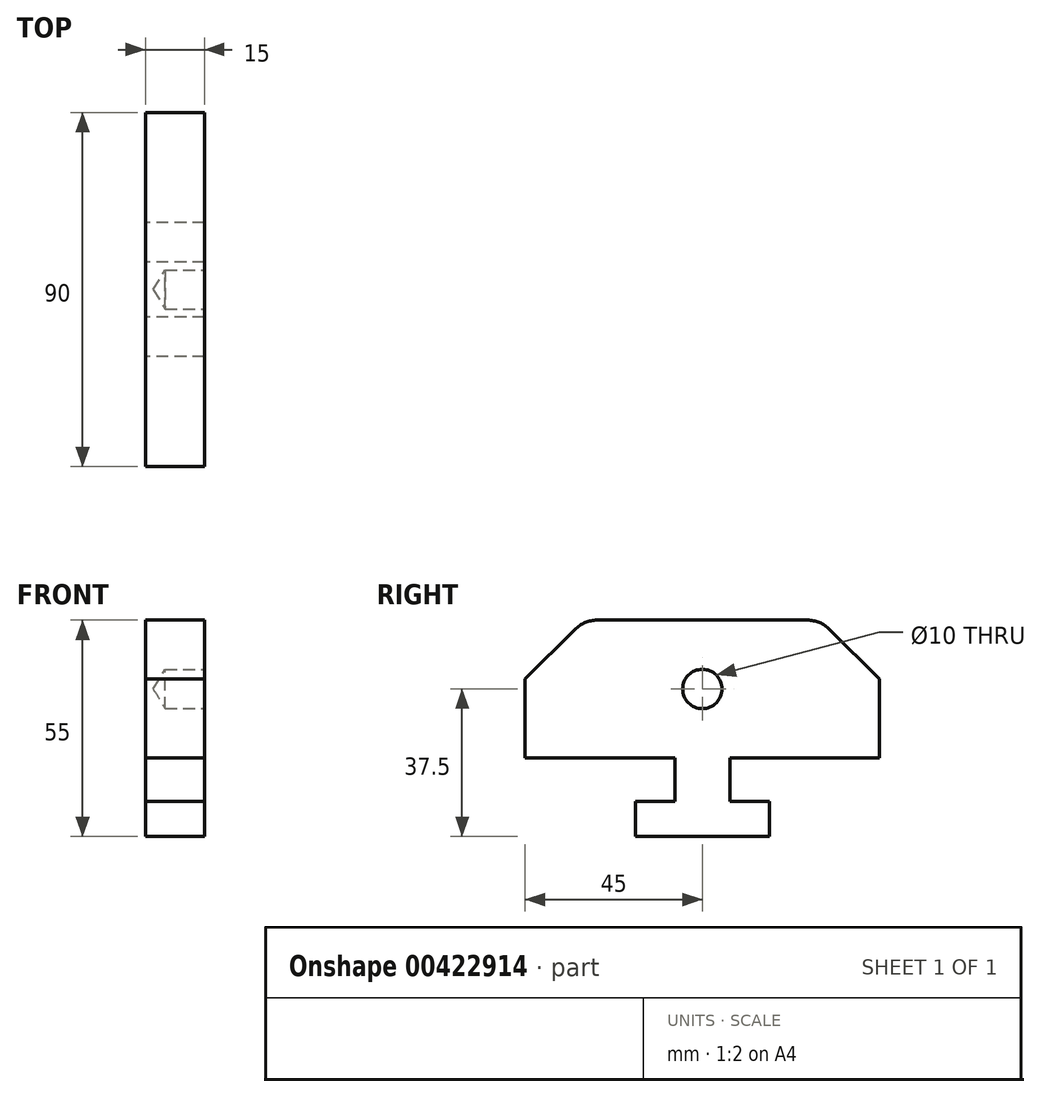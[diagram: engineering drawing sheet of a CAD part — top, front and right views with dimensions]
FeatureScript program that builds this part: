
annotation { "Feature Type Name" : "Feature", "Feature Type Description" : "" }
export const myFeature = defineFeature(function(context is Context, id is Id, definition is map)
    precondition{}
    {
        {
            var Q0;
            Q0=qCreatedBy(makeId("Right.planeOp"),FACE);
            var sketch = newSketch(context, id + "F0", { "sketchPlane" : qUnion([Q0])});
            skLineSegment(sketch, "E0", {"start": v(-17, 9) * mm, "end": v(-17, 0) * mm});
            skLineSegment(sketch, "E1", {"start": v(-17, 0) * mm, "end": v(17, 0) * mm});
            skLineSegment(sketch, "E2", {"start": v(17, 0) * mm, "end": v(17, 9) * mm});
            skLineSegment(sketch, "E3", {"start": v(-17, 9) * mm, "end": v(-7, 9) * mm});
            skLineSegment(sketch, "E4", {"start": v(-7, 9) * mm, "end": v(-7, 20) * mm});
            skLineSegment(sketch, "E5", {"start": v(-7, 20) * mm, "end": v(7, 20) * mm});
            skLineSegment(sketch, "E6", {"start": v(7, 20) * mm, "end": v(7, 9) * mm});
            skLineSegment(sketch, "E7", {"start": v(7, 9) * mm, "end": v(17, 9) * mm});
            skPoint(sketch, "E8.endSnap0", {"position": v(0, 20) * mm});
            skLineSegment(sketch, "E9", {"start": v(-26.69, 55) * mm, "end": v(26.69, 55) * mm});
            skLineSegment(sketch, "E10", {"start": v(-45, 20) * mm, "end": v(45, 20) * mm});
            skLineSegment(sketch, "E11", {"start": v(45, 20) * mm, "end": v(45, 40) * mm});
            skLineSegment(sketch, "E12", {"start": v(45, 40) * mm, "end": v(32.34, 52.66) * mm});
            skLineSegment(sketch, "E13", {"start": v(-45, 20) * mm, "end": v(-45, 40) * mm});
            skLineSegment(sketch, "E14", {"start": v(-45, 40) * mm, "end": v(-32.34, 52.66) * mm});
            skPoint(sketch, "E15.visualSharp", {"position": v(-30, 55) * mm});
            skArc(sketch, "E15.filletArc", {"start": v(-26.69, 55) * mm, "mid": v(-29.75, 54.4) * mm, "end": v(-32.34, 52.66) * mm});
            skPoint(sketch, "E16.visualSharp", {"position": v(30, 55) * mm});
            skArc(sketch, "E16.filletArc", {"start": v(32.34, 52.66) * mm, "mid": v(29.75, 54.4) * mm, "end": v(26.69, 55) * mm});
            skPoint(sketch, "E17", {"position": v(0, 37.5) * mm});
            skSolve(sketch);
        }
        {
            var Q0;
            Q0 = qSketchRegion(id + "F0", true);
            extrude(context, id + "F1", {"entities" : qUnion([Q0]), "depth" : 15 * mm});
        }
        {
            var Q0;
            Q0=makeQuery(id+"F1.opExtrude","CAP_FACE",FACE,{"disambiguationData":[OSD([sQuery(id+"F0.wireOp",EDGE,"E0"),sQuery(id+"F0.wireOp",EDGE,"E1"),sQuery(id+"F0.wireOp",EDGE,"E2"),sQuery(id+"F0.wireOp",EDGE,"E3"),sQuery(id+"F0.wireOp",EDGE,"E4"),sQuery(id+"F0.wireOp",EDGE,"E6"),sQuery(id+"F0.wireOp",EDGE,"E7"),sQuery(id+"F0.wireOp",EDGE,"E9"),sQuery(id+"F0.wireOp",EDGE,"E10"),sQuery(id+"F0.wireOp",EDGE,"E11"),sQuery(id+"F0.wireOp",EDGE,"E12"),sQuery(id+"F0.wireOp",EDGE,"E13"),sQuery(id+"F0.wireOp",EDGE,"E14"),sQuery(id+"F0.wireOp",EDGE,"E15.filletArc"),sQuery(id+"F0.wireOp",EDGE,"E16.filletArc")])],"isStart":false});
            var sketch = newSketch(context, id + "F2", { "sketchPlane" : qUnion([Q0])});
            skLineSegment(sketch, "E18", {"start": v(0, 0) * mm, "end": v(0, 37.5) * mm, "construction": true});
            skSolve(sketch);
        }
        {
            var Q0;
            Q0=sQuery(id+"F2.wireOp",VERTEX,"E18.end");
            var Q1;
            Q1=makeQuery(id+"F1.opExtrude","SWEPT_BODY",BODY,{"disambiguationData":[OSD([sQuery(id+"F0.wireOp",EDGE,"E0"),sQuery(id+"F0.wireOp",EDGE,"E1"),sQuery(id+"F0.wireOp",EDGE,"E2"),sQuery(id+"F0.wireOp",EDGE,"E3"),sQuery(id+"F0.wireOp",EDGE,"E4"),sQuery(id+"F0.wireOp",EDGE,"E6"),sQuery(id+"F0.wireOp",EDGE,"E7"),sQuery(id+"F0.wireOp",EDGE,"E9"),sQuery(id+"F0.wireOp",EDGE,"E10"),sQuery(id+"F0.wireOp",EDGE,"E11"),sQuery(id+"F0.wireOp",EDGE,"E12"),sQuery(id+"F0.wireOp",EDGE,"E13"),sQuery(id+"F0.wireOp",EDGE,"E14"),sQuery(id+"F0.wireOp",EDGE,"E15.filletArc"),sQuery(id+"F0.wireOp",EDGE,"E16.filletArc")])]});
            hole(context, id + "F3", {"style" : HoleStyle.SIMPLE, "endStyle" : HoleEndStyle.BLIND, "holeDiameter" : 10 * mm, "holeDepth" : 10 * mm, "isTappedThrough" : true, "tappedDepth" : 12 * mm, "tapClearance" : 3, "locations" : qUnion([Q0]), "scope" : qUnion([Q1])});
        }
    });
